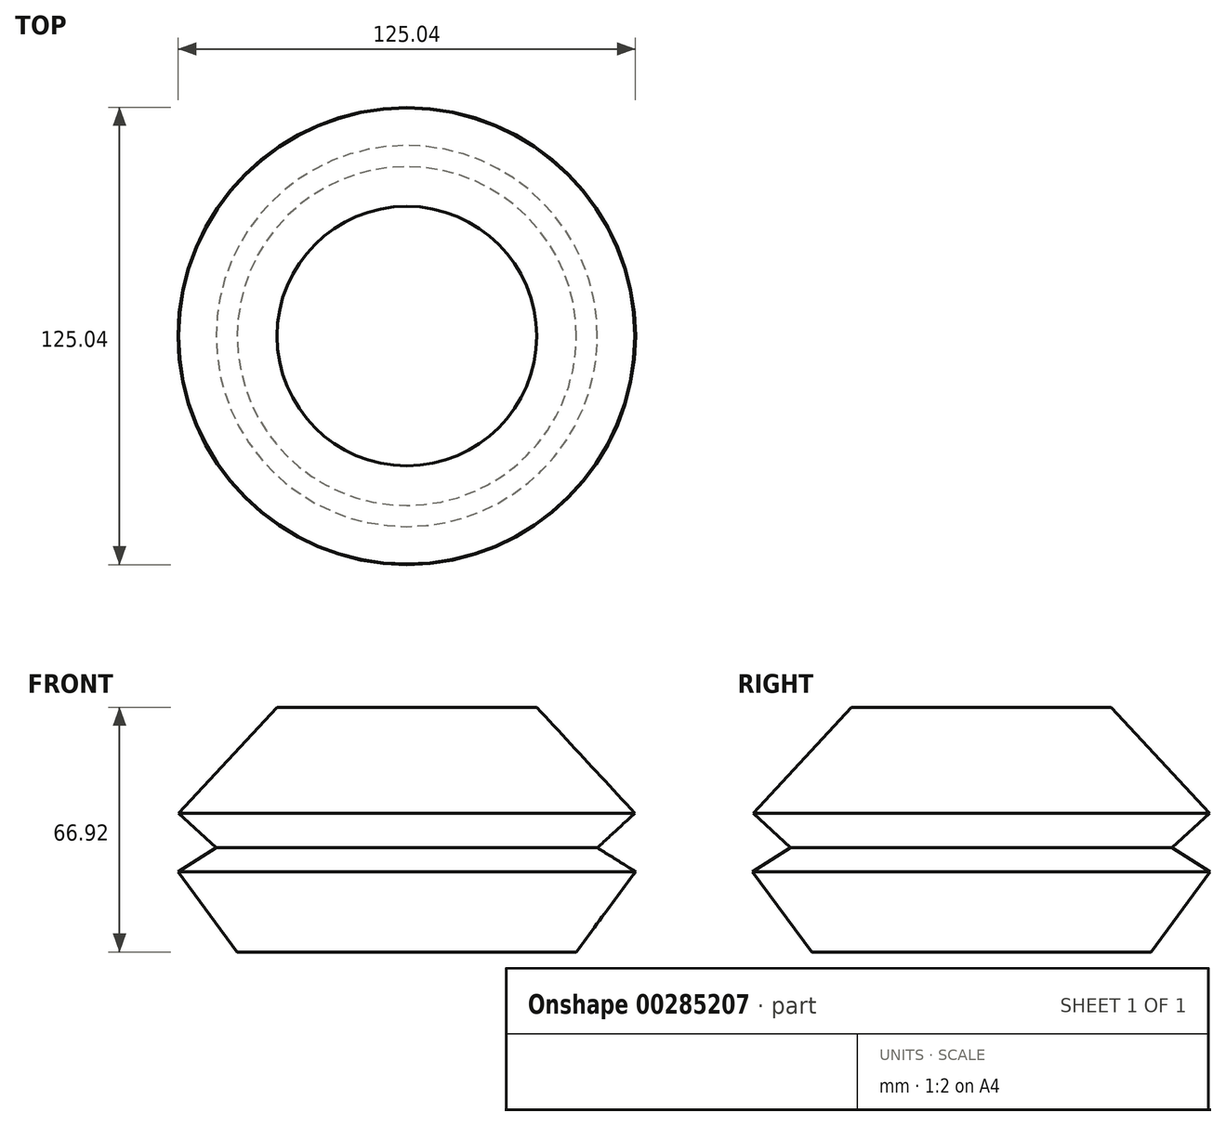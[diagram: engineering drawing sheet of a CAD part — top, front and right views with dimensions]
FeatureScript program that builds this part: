
annotation { "Feature Type Name" : "Feature", "Feature Type Description" : "" }
export const myFeature = defineFeature(function(context is Context, id is Id, definition is map)
    precondition{}
    {
        {
            var Q0;
            Q0=qCreatedBy(makeId("Front.planeOp"),FACE);
            var sketch = newSketch(context, id + "F0", { "sketchPlane" : qUnion([Q0])});
            skLineSegment(sketch, "E0", {"start": v(-46.34, 0) * mm, "end": v(0, 0) * mm});
            skLineSegment(sketch, "E1", {"start": v(0, 0) * mm, "end": v(-46.34, 0) * mm});
            skLineSegment(sketch, "E2", {"start": v(-62.52, 21.96) * mm, "end": v(-46.34, 0) * mm});
            skLineSegment(sketch, "E3", {"start": v(-52.1, 28.47) * mm, "end": v(-62.52, 21.96) * mm});
            skLineSegment(sketch, "E4", {"start": v(-62.33, 37.96) * mm, "end": v(-52.1, 28.47) * mm});
            skLineSegment(sketch, "E5", {"start": v(-62.33, 37.96) * mm, "end": v(-35.48, 66.92) * mm});
            skLineSegment(sketch, "E6", {"start": v(-35.48, 66.92) * mm, "end": v(0, 66.92) * mm});
            skLineSegment(sketch, "E7", {"start": v(0, 66.92) * mm, "end": v(0, 0) * mm});
            skLineSegment(sketch, "E8", {"start": v(0, 28.47) * mm, "end": v(-52.1, 28.47) * mm});
            skSolve(sketch);
        }
        {
            var Q0;
            Q0 = qSketchRegion(id + "F0", true);
            var Q1;
            Q1=sQuery(id+"F0.wireOp",EDGE,"E7");
            revolve(context, id + "F1", {"entities" : qUnion([Q0]), "axis" : qUnion([Q1]), "revolveType" : RevolveType.FULL});
        }
    });
